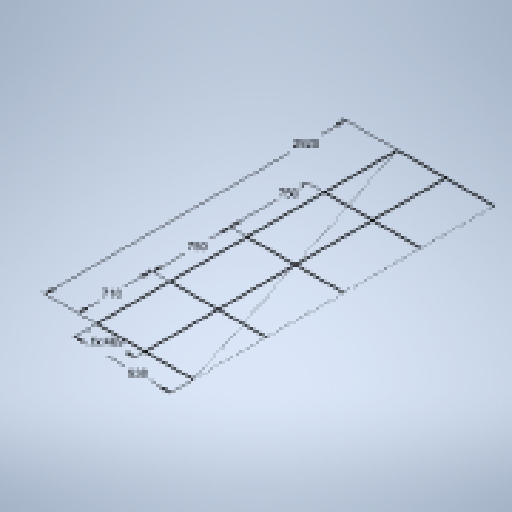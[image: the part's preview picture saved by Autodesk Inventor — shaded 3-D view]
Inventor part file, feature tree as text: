
AUTODESK INVENTOR PART (.ipt)
format: ipt  version: 2025 (Build 290162010, 162A)  size: 138,240 bytes
history: native  units: in
note: dims shown in document units (in); Inventor stores cm internally (conversion verified against a paired STEP export)
features: sketch x1
ambient origin geometry x8: Origin, YZ Plane, XZ Plane, XY Plane, X Axis, Y Axis, Z Axis, Center Point
feature tree (1):
  sketch  "Sketch3"  dims[d7=36.9291in d8=49.2126in d24=18.4646in d25=114.9606in d26=27.9528in d29=29.5276in d30=29.5276in]
